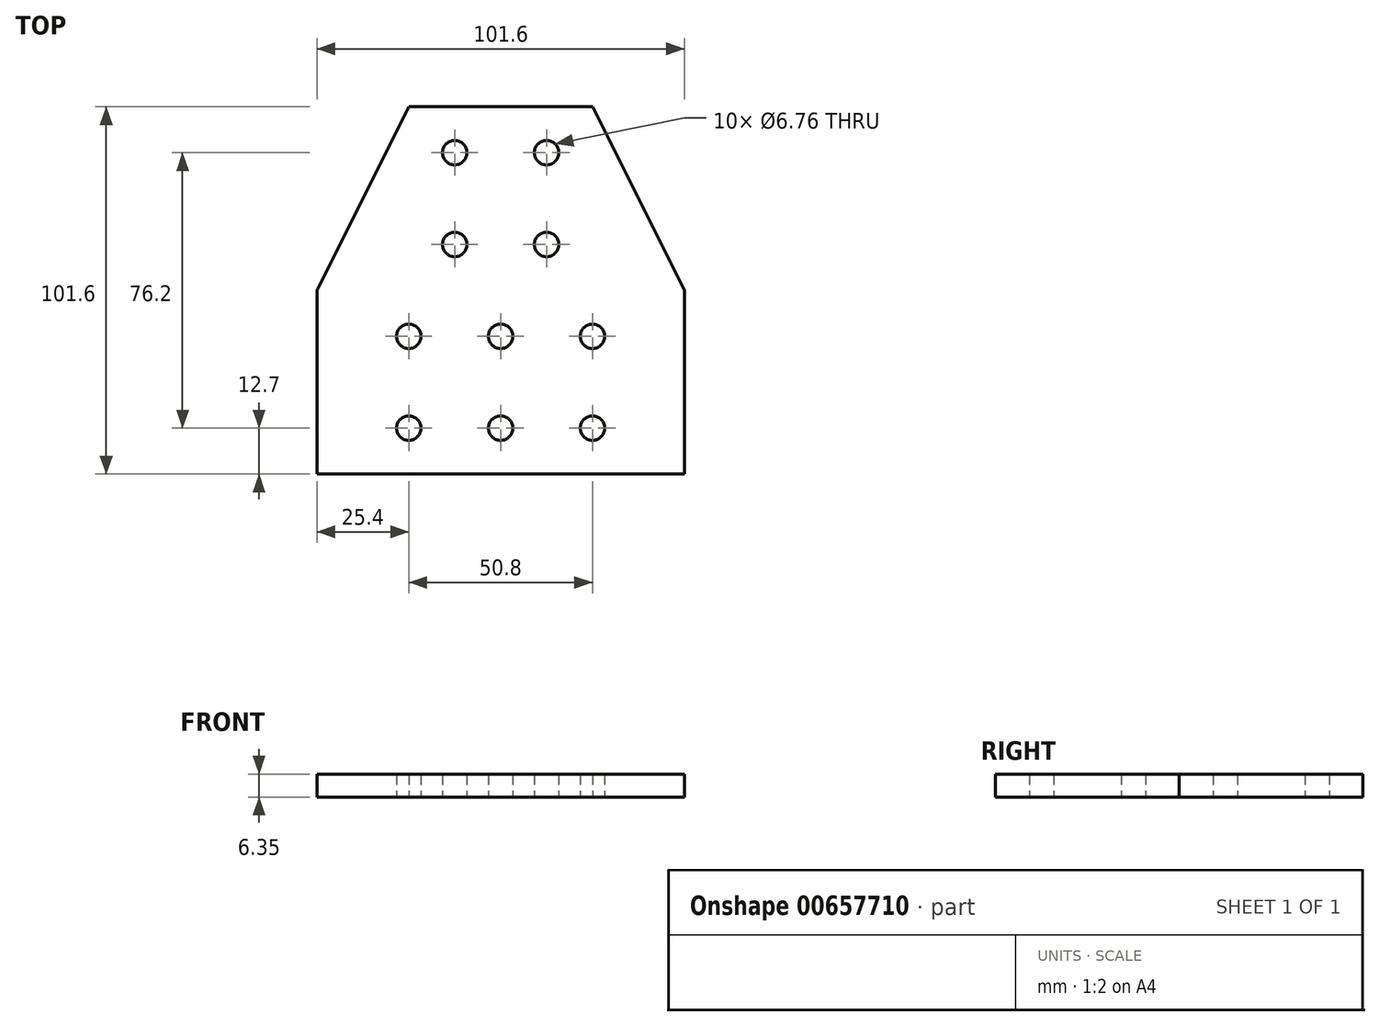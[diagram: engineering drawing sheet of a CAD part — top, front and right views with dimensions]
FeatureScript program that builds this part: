
annotation { "Feature Type Name" : "Feature", "Feature Type Description" : "" }
export const myFeature = defineFeature(function(context is Context, id is Id, definition is map)
    precondition{}
    {
        {
            var Q0;
            Q0=qCreatedBy(makeId("Top.planeOp"),FACE);
            var sketch = newSketch(context, id + "F0", { "sketchPlane" : qUnion([Q0])});
            skLineSegment(sketch, "E0.bottom", {"start": v(0, 0) * mm, "end": v(101.6, 0) * mm});
            skLineSegment(sketch, "E0.top", {"start": v(0, -101.6) * mm, "end": v(101.6, -101.6) * mm});
            skLineSegment(sketch, "E0.left", {"start": v(0, 0) * mm, "end": v(0, -101.6) * mm});
            skLineSegment(sketch, "E0.right", {"start": v(101.6, 0) * mm, "end": v(101.6, -101.6) * mm});
            skLineSegment(sketch, "E1", {"start": v(25.4, 0) * mm, "end": v(0, -50.8) * mm});
            skLineSegment(sketch, "E2", {"start": v(76.2, 0) * mm, "end": v(101.6, -50.8) * mm});
            skCircle(sketch, "E3", {"center": v(38.1, -12.7) * mm, "radius": 3.38 * mm});
            skCircle(sketch, "E4.0.1.0", {"center": v(38.1, -38.1) * mm, "radius": 3.38 * mm});
            skCircle(sketch, "E4.1.0.0", {"center": v(63.5, -12.7) * mm, "radius": 3.38 * mm});
            skCircle(sketch, "E4.1.1.0", {"center": v(63.5, -38.1) * mm, "radius": 3.38 * mm});
            skLineSegment(sketch, "E4.direction1", {"start": v(38.1, -12.7) * mm, "end": v(63.5, -12.7) * mm, "construction": true});
            skLineSegment(sketch, "E4.direction2", {"start": v(38.1, -12.7) * mm, "end": v(38.1, -38.1) * mm, "construction": true});
            skCircle(sketch, "E5", {"center": v(25.4, -63.5) * mm, "radius": 3.38 * mm});
            skCircle(sketch, "E6.0.1.0", {"center": v(25.4, -88.9) * mm, "radius": 3.38 * mm});
            skCircle(sketch, "E6.1.0.0", {"center": v(50.8, -63.5) * mm, "radius": 3.38 * mm});
            skCircle(sketch, "E6.1.1.0", {"center": v(50.8, -88.9) * mm, "radius": 3.38 * mm});
            skCircle(sketch, "E6.2.0.0", {"center": v(76.2, -63.5) * mm, "radius": 3.38 * mm});
            skCircle(sketch, "E6.2.1.0", {"center": v(76.2, -88.9) * mm, "radius": 3.38 * mm});
            skLineSegment(sketch, "E6.direction1", {"start": v(25.4, -63.5) * mm, "end": v(50.8, -63.5) * mm, "construction": true});
            skLineSegment(sketch, "E6.direction2", {"start": v(25.4, -63.5) * mm, "end": v(25.4, -88.9) * mm, "construction": true});
            skSolve(sketch);
        }
        {
            var Q0;
            {var subQ3=sQuery(id+"F0.wireOp",EDGE,"E0.top");Q0=makeQuery(id+"F0.imprint","IMPRINT",FACE,{"disambiguationData":[TD([[makeQuery(id+"F0.imprint","IMPRINT",EDGE,{"derivedFrom":subQ3}),1.0]])]});}
            extrude(context, id + "F1", {"entities" : qUnion([Q0]), "depth" : 6.35 * mm, "offsetDistance" : 25.4 * mm});
        }
    });
